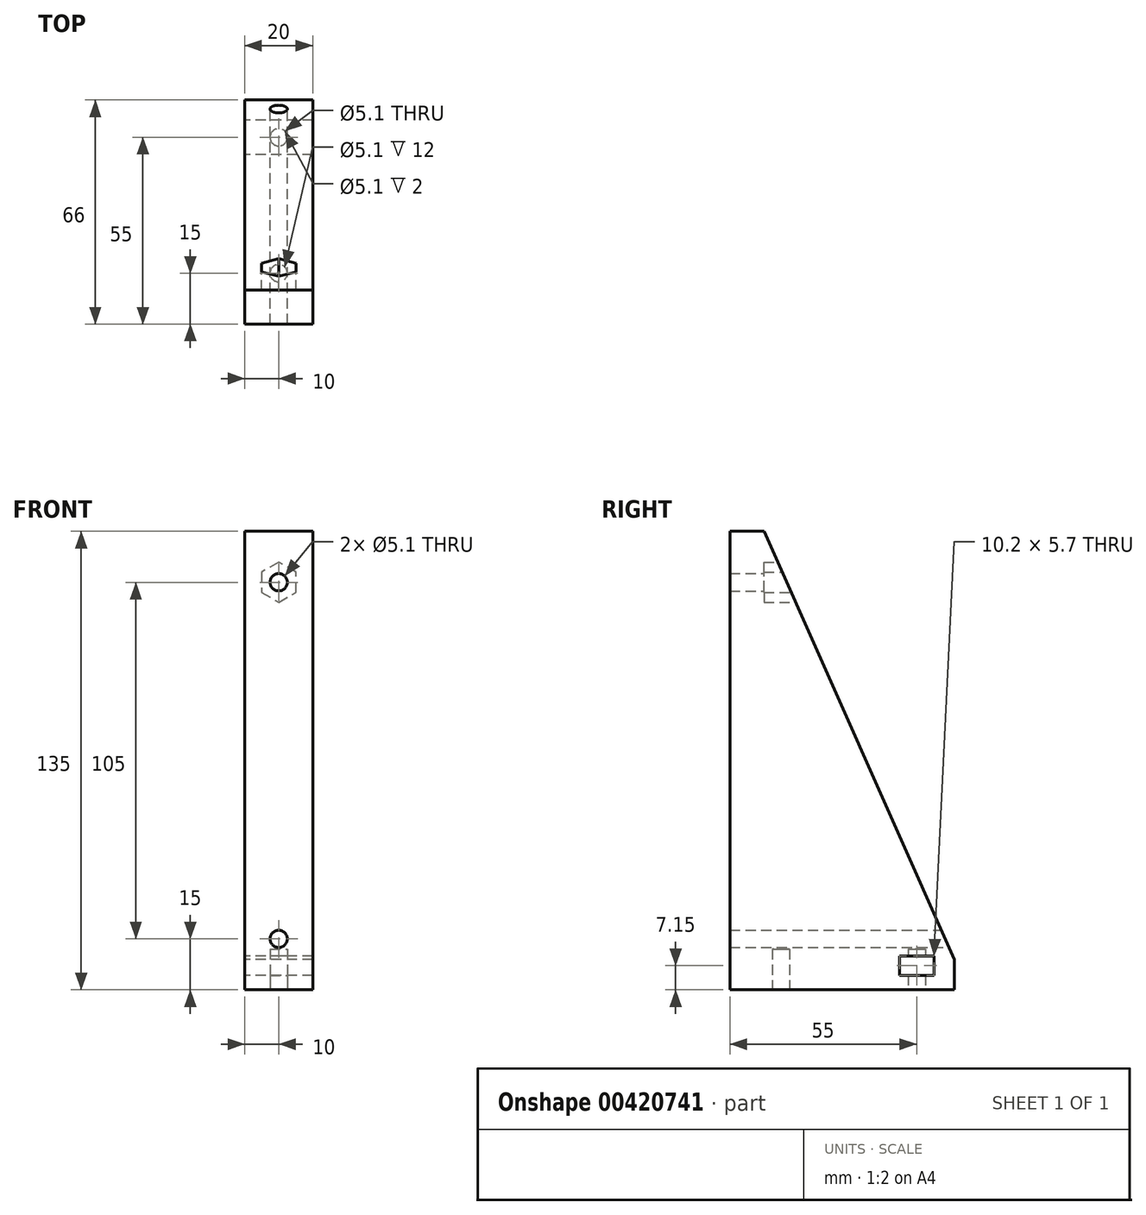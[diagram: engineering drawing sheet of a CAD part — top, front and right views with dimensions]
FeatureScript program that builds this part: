
annotation { "Feature Type Name" : "Feature", "Feature Type Description" : "" }
export const myFeature = defineFeature(function(context is Context, id is Id, definition is map)
    precondition{}
    {
        {
            var Q0;
            Q0=qCreatedBy(makeId("Right.planeOp"),FACE);
            var sketch = newSketch(context, id + "F0", { "sketchPlane" : qUnion([Q0])});
            skLineSegment(sketch, "E0", {"start": v(0, 0) * mm, "end": v(-70, 0) * mm});
            skLineSegment(sketch, "E1", {"start": v(-70, 0) * mm, "end": v(-70, 135) * mm});
            skLineSegment(sketch, "E2", {"start": v(-70, 135) * mm, "end": v(-60, 135) * mm});
            skLineSegment(sketch, "E3", {"start": v(-60, 135) * mm, "end": v(0, 0) * mm});
            skSolve(sketch);
        }
        {
            var Q0;
            Q0=qSketchRegion(id+"F0",true);
            extrude(context, id + "F1", {"entities" : qUnion([Q0]), "depth" : 20 * mm});
        }
        {
            var Q0;
            Q0=makeQuery(id+"F1.opExtrude","SWEPT_FACE",FACE,{"disambiguationData":[OSD([sQuery(id+"F0.wireOp",EDGE,"E1")])]});
            var sketch = newSketch(context, id + "F2", { "sketchPlane" : qUnion([Q0])});
            skLineSegment(sketch, "E4", {"start": v(10, 135) * mm, "end": v(10, 120) * mm});
            skLineSegment(sketch, "E5", {"start": v(10, 0) * mm, "end": v(10, 15) * mm});
            skPoint(sketch, "E6.0.midPoint", {"position": v(16.6, 120) * mm});
            skCircle(sketch, "E7.cCircle", {"center": v(10, 15) * mm, "radius": 5.1 * mm, "construction": true});
            skLineSegment(sketch, "E7.0", {"start": v(4.9, 12.06) * mm, "end": v(4.9, 17.94) * mm});
            skLineSegment(sketch, "E7.1", {"start": v(4.9, 17.94) * mm, "end": v(10, 20.89) * mm});
            skLineSegment(sketch, "E7.2", {"start": v(10, 20.89) * mm, "end": v(15.1, 17.94) * mm});
            skLineSegment(sketch, "E7.3", {"start": v(15.1, 17.94) * mm, "end": v(15.1, 12.06) * mm});
            skLineSegment(sketch, "E7.4", {"start": v(15.1, 12.06) * mm, "end": v(10, 9.11) * mm});
            skLineSegment(sketch, "E7.5", {"start": v(10, 9.11) * mm, "end": v(4.9, 12.06) * mm});
            skPoint(sketch, "E7.0.midPoint", {"position": v(4.9, 15) * mm});
            skCircle(sketch, "E8.cCircle", {"center": v(10, 120) * mm, "radius": 5.1 * mm, "construction": true});
            skLineSegment(sketch, "E8.0", {"start": v(4.9, 117.06) * mm, "end": v(4.9, 122.94) * mm});
            skLineSegment(sketch, "E8.1", {"start": v(4.9, 122.94) * mm, "end": v(10, 125.89) * mm});
            skLineSegment(sketch, "E8.2", {"start": v(10, 125.89) * mm, "end": v(15.1, 122.94) * mm});
            skLineSegment(sketch, "E8.3", {"start": v(15.1, 122.94) * mm, "end": v(15.1, 117.06) * mm});
            skLineSegment(sketch, "E8.4", {"start": v(15.1, 117.06) * mm, "end": v(10, 114.11) * mm});
            skLineSegment(sketch, "E8.5", {"start": v(10, 114.11) * mm, "end": v(4.9, 117.06) * mm});
            skPoint(sketch, "E8.0.midPoint", {"position": v(4.9, 120) * mm});
            skSolve(sketch);
        }
        {
            var Q0;
            Q0=sQuery(id+"F2.wireOp",VERTEX,"E5.end");
            var Q1;
            Q1=sQuery(id+"F2.wireOp",VERTEX,"E4.end");
            var Q2;
            Q2=makeQuery(id+"F1.opExtrude","SWEPT_BODY",BODY,{"disambiguationData":[OSD([sQuery(id+"F0.wireOp",EDGE,"E0"),sQuery(id+"F0.wireOp",EDGE,"E1"),sQuery(id+"F0.wireOp",EDGE,"E2"),sQuery(id+"F0.wireOp",EDGE,"E3")])]});
            hole(context, id + "F3", {"style" : HoleStyle.SIMPLE, "endStyle" : HoleEndStyle.THROUGH, "holeDiameter" : 5.1 * mm, "isTappedThrough" : true, "tappedDepth" : 12 * mm, "tapClearance" : 3, "locations" : qUnion([Q0, Q1]), "scope" : qUnion([Q2]), "startStyle" : HoleStartStyle.PART});
        }
        {
            var Q0;
            Q0=makeQuery(id+"F1.opExtrude","SWEPT_FACE",FACE,{"disambiguationData":[OSD([sQuery(id+"F0.wireOp",EDGE,"E0")])]});
            var sketch = newSketch(context, id + "F4", { "sketchPlane" : qUnion([Q0])});
            skLineSegment(sketch, "E9", {"start": v(10, 70) * mm, "end": v(10, 55) * mm});
            skLineSegment(sketch, "E10", {"start": v(10, 55) * mm, "end": v(10, 15) * mm});
            skPoint(sketch, "E10.endSnap0", {"position": v(10, 0) * mm});
            skCircle(sketch, "E11", {"center": v(10, 55) * mm, "radius": 2.55 * mm});
            skCircle(sketch, "E12", {"center": v(10, 15) * mm, "radius": 2.55 * mm});
            skLineSegment(sketch, "E13", {"start": v(10, 0) * mm, "end": v(10, 4) * mm});
            skLineSegment(sketch, "E14", {"start": v(10, 4) * mm, "end": v(20, 4) * mm});
            skLineSegment(sketch, "E15", {"start": v(20, 4) * mm, "end": v(0, 4) * mm});
            skSolve(sketch);
        }
        {
            var Q0;
            Q0=qSketchRegion(id+"F4",true);
            extrude(context, id + "F5", {"entities" : qUnion([Q0]), "operationType" : NewBodyOperationType.REMOVE, "oppositeDirection" : true, "depth" : 12 * mm});
        }
        {
            var Q0;
            Q0=makeQuery(id+"F2.imprint","IMPRINT",FACE,{"disambiguationData":[TD([[makeQuery(id+"F2.imprint","IMPRINT",EDGE,{"derivedFrom":sQuery(id+"F2.wireOp",EDGE,"E6.0")}),-1.0]])]});
            var Q1;
            Q1=makeQuery(id+"F2.imprint","IMPRINT",FACE,{"disambiguationData":[TD([[makeQuery(id+"F2.imprint","IMPRINT",EDGE,{"derivedFrom":sQuery(id+"F2.wireOp",EDGE,"E8.0")}),-1.0]])]});
            extrude(context, id + "F6", {"entities" : qUnion([Q0, Q1]), "operationType" : NewBodyOperationType.ADD, "oppositeDirection" : true, "depth" : 25 * mm});
        }
        {
            var Q0;
            Q0=makeQuery(id+"F6.opExtrude","CAP_FACE",FACE,{"disambiguationData":[OSD([sQuery(id+"F2.wireOp",EDGE,"E6.0"),sQuery(id+"F2.wireOp",EDGE,"E6.1"),sQuery(id+"F2.wireOp",EDGE,"E6.2"),sQuery(id+"F2.wireOp",EDGE,"E6.3"),sQuery(id+"F2.wireOp",EDGE,"E6.4"),sQuery(id+"F2.wireOp",EDGE,"E6.5")])],"isStart":false});
            var Q1;
            Q1=makeQuery(id+"F6.opExtrude","CAP_FACE",FACE,{"disambiguationData":[OSD([sQuery(id+"F2.wireOp",EDGE,"E8.0"),sQuery(id+"F2.wireOp",EDGE,"E8.1"),sQuery(id+"F2.wireOp",EDGE,"E8.2"),sQuery(id+"F2.wireOp",EDGE,"E8.3"),sQuery(id+"F2.wireOp",EDGE,"E8.4"),sQuery(id+"F2.wireOp",EDGE,"E8.5")])],"isStart":false});
            extrude(context, id + "F7", {"entities" : qUnion([Q0, Q1]), "operationType" : NewBodyOperationType.REMOVE, "oppositeDirection" : true, "depth" : 15 * mm});
        }
        {
            var Q0;
            Q0=sQuery(id+"F2.wireOp",VERTEX,"E4.end");
            var Q1;
            Q1=makeQuery(id+"F1.opExtrude","SWEPT_BODY",BODY,{"disambiguationData":[OSD([sQuery(id+"F0.wireOp",EDGE,"E0"),sQuery(id+"F0.wireOp",EDGE,"E1"),sQuery(id+"F0.wireOp",EDGE,"E2"),sQuery(id+"F0.wireOp",EDGE,"E3")])]});
            hole(context, id + "F8", {"style" : HoleStyle.SIMPLE, "endStyle" : HoleEndStyle.THROUGH, "holeDiameter" : 5.1 * mm, "isTappedThrough" : true, "tappedDepth" : 12 * mm, "tapClearance" : 3, "locations" : qUnion([Q0]), "scope" : qUnion([Q1]), "startStyle" : HoleStartStyle.PART});
        }
        {
            var Q0;
            Q0=makeQuery(id+"F1.opExtrude","CAP_FACE",FACE,{"disambiguationData":[OSD([sQuery(id+"F0.wireOp",EDGE,"E0"),sQuery(id+"F0.wireOp",EDGE,"E1"),sQuery(id+"F0.wireOp",EDGE,"E2"),sQuery(id+"F0.wireOp",EDGE,"E3")])],"isStart":true});
            var sketch = newSketch(context, id + "F9", { "sketchPlane" : qUnion([Q0])});
            skLineSegment(sketch, "E16", {"start": v(0, 0) * mm, "end": v(15, 0) * mm});
            skLineSegment(sketch, "E17", {"start": v(15, 0) * mm, "end": v(15, 10) * mm});
            skLineSegment(sketch, "E18", {"start": v(15, 10) * mm, "end": v(9.9, 10) * mm});
            skLineSegment(sketch, "E19", {"start": v(9.9, 10) * mm, "end": v(9.9, 4.3) * mm});
            skLineSegment(sketch, "E20", {"start": v(9.9, 4.3) * mm, "end": v(20.1, 4.3) * mm});
            skLineSegment(sketch, "E21", {"start": v(20.1, 4.3) * mm, "end": v(20.1, 10) * mm});
            skLineSegment(sketch, "E22", {"start": v(20.1, 10) * mm, "end": v(15, 10) * mm});
            skSolve(sketch);
        }
        {
            var Q0;
            {var subQ0=sQuery(id+"F9.wireOp",EDGE,"E18");Q0=makeQuery(id+"F9.imprint","IMPRINT",FACE,{"disambiguationData":[TD([[makeQuery(id+"F9.imprint","IMPRINT",EDGE,{"derivedFrom":subQ0}),1.0]])]});}
            var Q1;
            {var subQ4=sQuery(id+"F9.wireOp",EDGE,"E21");Q1=makeQuery(id+"F9.imprint","IMPRINT",FACE,{"disambiguationData":[TD([[makeQuery(id+"F9.imprint","IMPRINT",EDGE,{"derivedFrom":subQ4}),1.0]])]});}
            extrude(context, id + "F10", {"entities" : qUnion([Q0, Q1]), "operationType" : NewBodyOperationType.REMOVE, "oppositeDirection" : true, "depth" : 25 * mm});
        }
        {
            var Q0;
            {var subQ0=sQuery(id+"F4.wireOp",EDGE,"E13");Q0=makeQuery(id+"F4.imprint","IMPRINT",FACE,{"disambiguationData":[TD([[makeQuery(id+"F4.imprint","IMPRINT",EDGE,{"derivedFrom":subQ0}),-1.0]])]});}
            var Q1;
            {var subQ0=sQuery(id+"F4.wireOp",EDGE,"E13");Q1=makeQuery(id+"F4.imprint","IMPRINT",FACE,{"disambiguationData":[TD([[makeQuery(id+"F4.imprint","IMPRINT",EDGE,{"derivedFrom":subQ0}),1.0]])]});}
            extrude(context, id + "F11", {"entities" : qUnion([Q0, Q1]), "operationType" : NewBodyOperationType.REMOVE, "oppositeDirection" : true, "depth" : 25 * mm});
        }
    });
